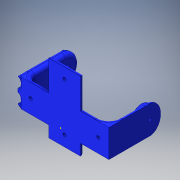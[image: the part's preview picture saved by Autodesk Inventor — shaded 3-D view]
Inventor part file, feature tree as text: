
AUTODESK INVENTOR PART (.ipt)
format: ipt  version: 2016 (Build 200138000, 138)  size: 574,976 bytes
history: native  units: in
note: dims shown in document units (in); Inventor stores cm internally (conversion verified against a paired STEP export)
features: sketch x13, other x3
ambient origin geometry x8: Origin, YZ Plane, XZ Plane, XY Plane, X Axis, Y Axis, Z Axis, Center Point
bodies: Solid1 (feature_tree)
feature tree (16):
  other  "Kne_v2.ipt"
  other  "Solid1::Kne_v2.ipt"
  other  "TaggingFeature1"
  sketch  "Sketch1"  dims[d0=0.3937in]
  sketch  "Sketch4"
  sketch  "Sketch5"
  sketch  "Sketch7"
  sketch  "Sketch9"
  sketch  "Sketch10"
  sketch  "Sketch15"
  sketch  "Sketch16"
  sketch  "Sketch17"
  sketch  "Sketch18"
  sketch  "Sketch19"
  sketch  "Sketch20"
  sketch  "Sketch21"
